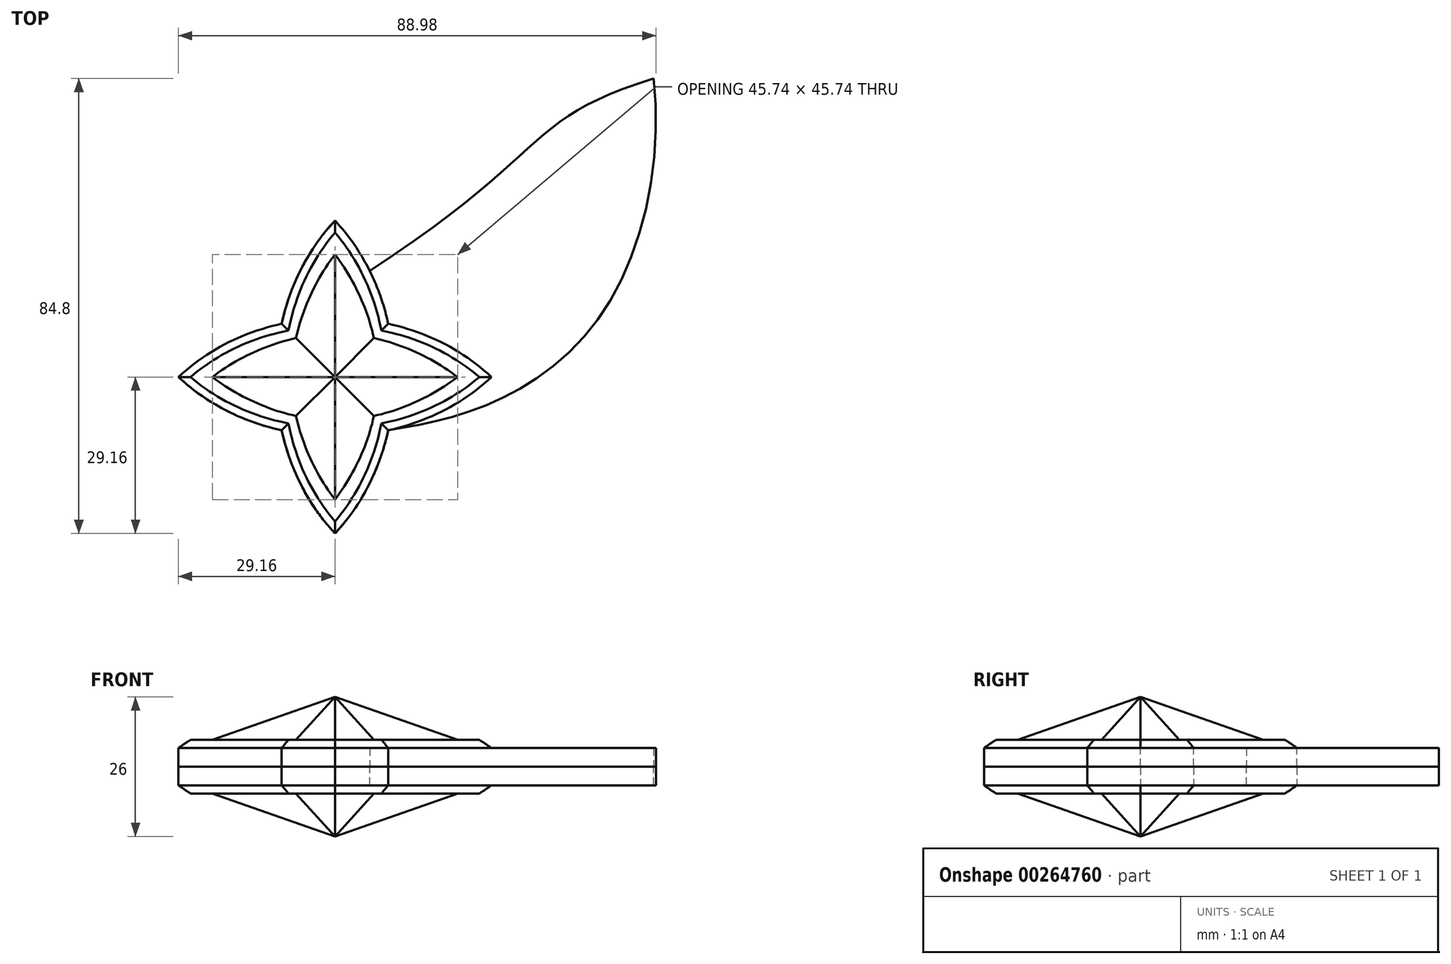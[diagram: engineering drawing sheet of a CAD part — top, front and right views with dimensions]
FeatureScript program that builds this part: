
annotation { "Feature Type Name" : "Feature", "Feature Type Description" : "" }
export const myFeature = defineFeature(function(context is Context, id is Id, definition is map)
    precondition{}
    {
        {
            var Q0;
            Q0=qCreatedBy(makeId("Top.planeOp"),FACE);
            var sketch = newSketch(context, id + "F0", { "sketchPlane" : qUnion([Q0])});
            skLineSegment(sketch, "E0", {"start": v(0, 25.42) * mm, "end": v(0, -24.58) * mm, "construction": true});
            skSolve(sketch);
        }
        {
            var Q0;
            Q0=qCreatedBy(makeId("Top.planeOp"),FACE);
            var sketch = newSketch(context, id + "F1", { "sketchPlane" : qUnion([Q0])});
            skFitSpline(sketch, "E1", {"points": [v(0, 22.87) * mm, v(-7.26, 7.26) * mm], "startDerivative": vector(-10.3, -13.5) * mm, "endDerivative": vector(-3.62, -16.65) * mm});
            skLineSegment(sketch, "E2", {"start": v(-7.26, 7.26) * mm, "end": v(0, 0) * mm, "construction": true});
            skFitSpline(sketch, "E3.MirrorCS", {"points": [v(0, 22.87) * mm, v(7.26, 7.26) * mm], "startDerivative": vector(10.3, -13.5) * mm, "endDerivative": vector(3.62, -16.65) * mm});
            skLineSegment(sketch, "E4.MirrorCS", {"start": v(7.26, 7.26) * mm, "end": v(0, 0) * mm, "construction": true});
            skFitSpline(sketch, "E5.MirrorCS", {"points": [v(-22.87, 0) * mm, v(-7.26, 7.26) * mm], "startDerivative": vector(13.5, 10.3) * mm, "endDerivative": vector(16.65, 3.62) * mm});
            skFitSpline(sketch, "E6.MirrorCS", {"points": [v(-22.87, 0) * mm, v(-7.26, -7.26) * mm], "startDerivative": vector(13.5, -10.3) * mm, "endDerivative": vector(16.65, -3.62) * mm});
            skFitSpline(sketch, "E7.MirrorCS", {"points": [v(22.87, 0) * mm, v(7.26, 7.26) * mm], "startDerivative": vector(-13.5, 10.3) * mm, "endDerivative": vector(-16.65, 3.62) * mm});
            skFitSpline(sketch, "E8.MirrorCS", {"points": [v(22.87, 0) * mm, v(7.26, -7.26) * mm], "startDerivative": vector(-13.5, -10.3) * mm, "endDerivative": vector(-16.65, -3.62) * mm});
            skFitSpline(sketch, "E9.MirrorCS", {"points": [v(0, -22.87) * mm, v(7.26, -7.26) * mm], "startDerivative": vector(10.3, 13.5) * mm, "endDerivative": vector(3.62, 16.65) * mm});
            skFitSpline(sketch, "E10.MirrorCS", {"points": [v(0, -22.87) * mm, v(-7.26, -7.26) * mm], "startDerivative": vector(-10.3, 13.5) * mm, "endDerivative": vector(-3.62, 16.65) * mm});
            skSolve(sketch);
        }
        {
            var Q0;
            Q0=qCreatedBy(makeId("Top.planeOp"),FACE);
            cPlane(context, id + "F2", {"entities" : qUnion([Q0]), "cplaneType" : CPlaneType.OFFSET, "offset" : 8 * mm, "width" : 150 * mm, "height" : 150 * mm});
        }
        {
            var Q0;
            Q0=qCreatedBy(id+"F2.planeOp",FACE);
            var sketch = newSketch(context, id + "F3", { "sketchPlane" : qUnion([Q0])});
            skPoint(sketch, "E11", {"position": v(0, 0) * mm});
            skSolve(sketch);
        }
        {
            var Q0;
            Q0=makeQuery(id+"F1.imprint","IMPRINT",FACE,{"disambiguationData":[TD([[makeQuery(id+"F1.imprint","IMPRINT",EDGE,{"derivedFrom":sQuery(id+"F1.wireOp",EDGE,"E1")}),1.0]])]});
            var Q1;
            Q1=sQuery(id+"F3.wireOp",VERTEX,"E11");
            loft(context, id + "F4", {"sheetProfilesArray" : [{ "sheetProfileEntities" : qUnion([Q0]) }, { "sheetProfileEntities" : qUnion([Q1]) }]});
        }
        {
            var Q0;
            Q0=qCreatedBy(makeId("Top.planeOp"),FACE);
            var sketch = newSketch(context, id + "F5", { "sketchPlane" : qUnion([Q0])});
            skFitSpline(sketch, "E12", {"points": [v(0, 29.16) * mm, v(-9.93, 9.93) * mm], "startDerivative": vector(-15.07, -16.03) * mm, "endDerivative": vector(-4.6, -21.32) * mm});
            skLineSegment(sketch, "E13", {"start": v(-9.93, 9.93) * mm, "end": v(0, 0) * mm, "construction": true});
            skFitSpline(sketch, "E14.MirrorCS", {"points": [v(0, 29.16) * mm, v(9.93, 9.93) * mm], "startDerivative": vector(15.07, -16.03) * mm, "endDerivative": vector(4.6, -21.32) * mm});
            skLineSegment(sketch, "E15.MirrorCS", {"start": v(9.93, 9.93) * mm, "end": v(0, 0) * mm, "construction": true});
            skFitSpline(sketch, "E16.MirrorCS", {"points": [v(-29.16, 0) * mm, v(-9.93, -9.93) * mm], "startDerivative": vector(16.03, -15.07) * mm, "endDerivative": vector(21.32, -4.6) * mm});
            skFitSpline(sketch, "E17.MirrorCS", {"points": [v(-29.16, 0) * mm, v(-9.93, 9.93) * mm], "startDerivative": vector(16.03, 15.07) * mm, "endDerivative": vector(21.32, 4.6) * mm});
            skFitSpline(sketch, "E18.MirrorCS", {"points": [v(29.16, 0) * mm, v(9.93, 9.93) * mm], "startDerivative": vector(-16.03, 15.07) * mm, "endDerivative": vector(-21.32, 4.6) * mm});
            skFitSpline(sketch, "E19.MirrorCS", {"points": [v(29.16, 0) * mm, v(9.93, -9.93) * mm], "startDerivative": vector(-16.03, -15.07) * mm, "endDerivative": vector(-21.32, -4.6) * mm});
            skFitSpline(sketch, "E20.MirrorCS", {"points": [v(0, -29.16) * mm, v(9.93, -9.93) * mm], "startDerivative": vector(15.07, 16.03) * mm, "endDerivative": vector(4.6, 21.32) * mm});
            skFitSpline(sketch, "E21.MirrorCS", {"points": [v(0, -29.16) * mm, v(-9.93, -9.93) * mm], "startDerivative": vector(-15.07, 16.03) * mm, "endDerivative": vector(-4.6, 21.32) * mm});
            skSolve(sketch);
        }
        {
            var Q0;
            Q0=makeQuery(id+"F5.imprint","IMPRINT",FACE,{"disambiguationData":[TD([[makeQuery(id+"F5.imprint","IMPRINT",EDGE,{"derivedFrom":sQuery(id+"F5.wireOp",EDGE,"E12")}),1.0]])]});
            extrude(context, id + "F6", {"entities" : qUnion([Q0]), "operationType" : NewBodyOperationType.ADD, "oppositeDirection" : true, "depth" : 5 * mm, "offsetDistance" : 25 * mm});
        }
        {
            var Q0;
            Q0=makeQuery(id+"F6.opExtrude","CAP_EDGE",EDGE,{"disambiguationData":[OSD([sQuery(id+"F5.wireOp",EDGE,"E17.MirrorCS")])],"isStart":true});
            var Q1;
            Q1=makeQuery(id+"F6.opExtrude","CAP_EDGE",EDGE,{"disambiguationData":[OSD([sQuery(id+"F5.wireOp",EDGE,"E16.MirrorCS")])],"isStart":true});
            var Q2;
            Q2=makeQuery(id+"F6.opExtrude","CAP_EDGE",EDGE,{"disambiguationData":[OSD([sQuery(id+"F5.wireOp",EDGE,"E21.MirrorCS")])],"isStart":true});
            var Q3;
            Q3=makeQuery(id+"F6.opExtrude","CAP_EDGE",EDGE,{"disambiguationData":[OSD([sQuery(id+"F5.wireOp",EDGE,"E20.MirrorCS")])],"isStart":true});
            var Q4;
            Q4=makeQuery(id+"F6.opExtrude","CAP_EDGE",EDGE,{"disambiguationData":[OSD([sQuery(id+"F5.wireOp",EDGE,"E19.MirrorCS")])],"isStart":true});
            var Q5;
            Q5=makeQuery(id+"F6.opExtrude","CAP_EDGE",EDGE,{"disambiguationData":[OSD([sQuery(id+"F5.wireOp",EDGE,"E18.MirrorCS")])],"isStart":true});
            var Q6;
            Q6=makeQuery(id+"F6.opExtrude","CAP_EDGE",EDGE,{"disambiguationData":[OSD([sQuery(id+"F5.wireOp",EDGE,"E14.MirrorCS")])],"isStart":true});
            var Q7;
            Q7=makeQuery(id+"F6.opExtrude","CAP_EDGE",EDGE,{"disambiguationData":[OSD([sQuery(id+"F5.wireOp",EDGE,"E12")])],"isStart":true});
            chamfer(context, id + "F7", {"entities" : qUnion([Q0, Q1, Q2, Q3, Q4, Q5, Q6, Q7]), "width" : 1.5 * mm, "tangentPropagation" : true});
        }
        {
            var Q0;
            Q0=makeQuery(id+"F6.opExtrude","CAP_FACE",FACE,{"disambiguationData":[OSD([sQuery(id+"F5.wireOp",EDGE,"E12"),sQuery(id+"F5.wireOp",EDGE,"E14.MirrorCS"),sQuery(id+"F5.wireOp",EDGE,"E16.MirrorCS"),sQuery(id+"F5.wireOp",EDGE,"E17.MirrorCS"),sQuery(id+"F5.wireOp",EDGE,"E18.MirrorCS"),sQuery(id+"F5.wireOp",EDGE,"E19.MirrorCS"),sQuery(id+"F5.wireOp",EDGE,"E20.MirrorCS"),sQuery(id+"F5.wireOp",EDGE,"E21.MirrorCS")])],"isStart":false});
            var sketch = newSketch(context, id + "F8", { "sketchPlane" : qUnion([Q0])});
            skFitSpline(sketch, "E22", {"points": [v(6.5, -19.77) * mm, v(59.36, -55.64) * mm], "startDerivative": vector(103.78, -67.74) * mm, "endDerivative": vector(73.35, -22.79) * mm});
            skFitSpline(sketch, "E23", {"points": [v(59.36, -55.64) * mm, v(57, -27.63) * mm, v(49.16, -12.44) * mm, v(41.09, -4.84) * mm, v(29.16, 0) * mm], "startDerivative": vector(7.23, 37.6) * mm, "endDerivative": vector(-63.74, 12.2) * mm, "construction": true});
            skFitSpline(sketch, "E24", {"points": [v(59.36, -55.64) * mm, v(50.8, -13.4) * mm, v(28.85, 5) * mm, v(9.93, 9.93) * mm], "startDerivative": vector(12.84, 109.7) * mm, "endDerivative": vector(-65.57, 10.73) * mm});
            skSolve(sketch);
        }
        {
            var Q0;
            {var subQ0=sQuery(id+"F8.wireOp",EDGE,"E22");Q0=makeQuery(id+"F8.imprint","IMPRINT",FACE,{"disambiguationData":[TD([[makeQuery(id+"F8.imprint","IMPRINT",EDGE,{"derivedFrom":subQ0}),1.0]])]});}
            extrude(context, id + "F9", {"entities" : qUnion([Q0]), "operationType" : NewBodyOperationType.ADD, "oppositeDirection" : true, "depth" : 3.5 * mm, "offsetDistance" : 25 * mm});
        }
        {
            var Q0;
            Q0=makeQuery(id+"F4.opLoft","SWEPT_BODY",BODY,{"disambiguationData":[OSD([makeQuery(id+"F1.imprint","IMPRINT",FACE,{"disambiguationData":[TD([[makeQuery(id+"F1.imprint","IMPRINT",EDGE,{"derivedFrom":sQuery(id+"F1.wireOp",EDGE,"E1")}),1.0]])]}),sQuery(id+"F3.wireOp",VERTEX,"E11")])]});
            var Q1;
            {var subQ0=sQuery(id+"F5.wireOp",EDGE,"E18.MirrorCS");var subQ1=sQuery(id+"F5.wireOp",EDGE,"E14.MirrorCS");Q1=makeQuery(id+"F9.boolean.opBoolean","MERGE",FACE,{"derivedFrom":[makeQuery(id+"F6.opExtrude","CAP_FACE",FACE,{"disambiguationData":[OSD([sQuery(id+"F5.wireOp",EDGE,"E12"),subQ1,sQuery(id+"F5.wireOp",EDGE,"E16.MirrorCS"),sQuery(id+"F5.wireOp",EDGE,"E17.MirrorCS"),subQ0,sQuery(id+"F5.wireOp",EDGE,"E19.MirrorCS"),sQuery(id+"F5.wireOp",EDGE,"E20.MirrorCS"),sQuery(id+"F5.wireOp",EDGE,"E21.MirrorCS")])],"isStart":false}),makeQuery(id+"F9.opExtrude","CAP_FACE",FACE,{"disambiguationData":[OSD([subQ1,subQ0,sQuery(id+"F8.wireOp",EDGE,"E22"),sQuery(id+"F8.wireOp",EDGE,"E23")])],"isStart":true})]});}
            mirror(context, id + "F10", {"entities" : qUnion([Q0]), "mirrorPlane" : qUnion([Q1])});
        }
    });
